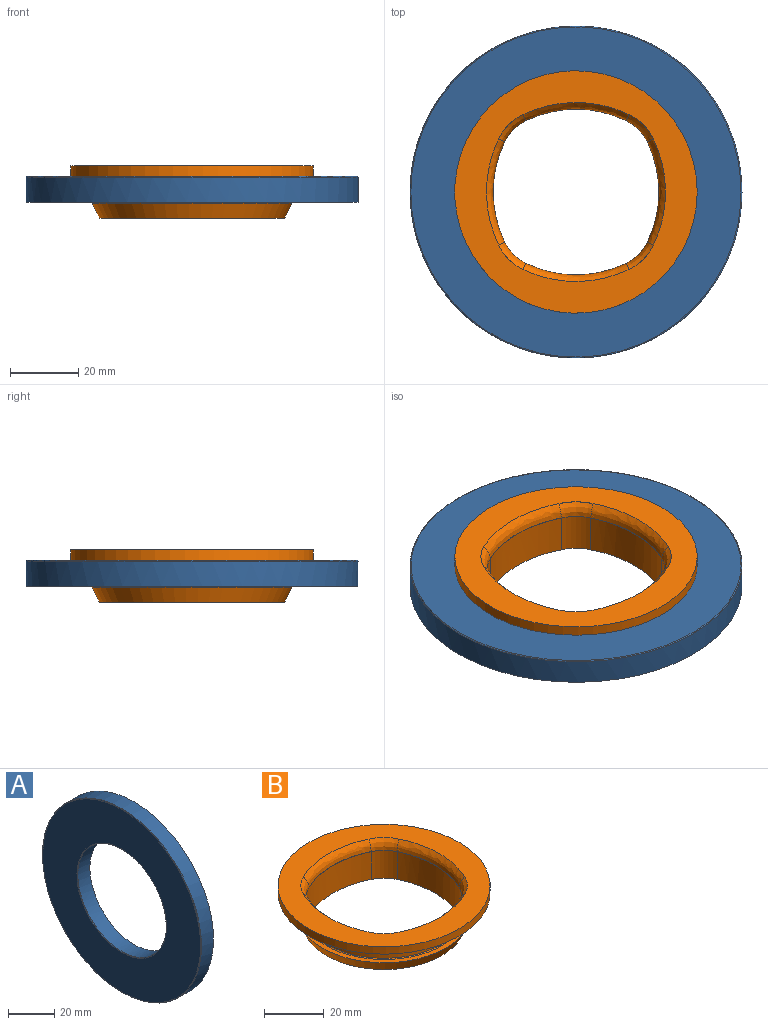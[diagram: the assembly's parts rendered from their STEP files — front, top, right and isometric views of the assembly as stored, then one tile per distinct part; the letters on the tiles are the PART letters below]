
ASSEMBLY  parts=2 mates=1
PART A: 12 faces, bbox 7.6x105x105 mm
  f0: plane 97.03x97.03mm, normal (1,0,0), area 230.5mm2, adj f1,f7
  f1: cylinder r=48.51mm len=97.03mm, axis (-1,0,0), area 2245.3mm2, adj f0,f8
  f2: plane 96.52x96.52mm, normal (-1,0,0), area 4974.6mm2, adj f8,f9
  f3: cylinder r=27.05mm len=54.1mm, axis (-1,0,0), area 1252mm2, adj f4,f9
  f4: plane 55.63x55.63mm, normal (1,0,0), area 131.3mm2, adj f3,f5
  f5: cylinder r=27.81mm len=55.63mm, axis (-1,0,0), area 1154.1mm2, adj f4,f10
  f6: plane 95x95mm, normal (1,0,0), area 4612.8mm2, adj f10,f11
  f7: cylinder r=47.75mm len=95.5mm, axis (-1,0,0), area 1981.4mm2, adj f0,f11
  f8: torus R=48.26mm, axis (1,0,0), area 121.4mm2, adj f1,f2
  f9: torus R=27.3mm, axis (1,0,0), area 68mm2, adj f2,f3
  f10: torus R=28.07mm, axis (-1,0,0), area 70mm2, adj f5,f6
  f11: torus R=47.5mm, axis (-1,0,0), area 119.5mm2, adj f6,f7
PART B: 42 faces, bbox 70.9x70.9x15.3 mm
  f0: bspline ~6.56x6.56mm, area 0mm2, adj f1,f41
  f1: plane 70.88x70.88mm, normal (0,0,1), area 1680.9mm2, adj f0,f2,f27,f28,f30,f31,f32,f34
  f2: cylinder r=35.43mm len=70.87mm, axis (0,0,1), area 667.3mm2, adj f1,f3
  f3: plane 70.87x70.87mm, normal (0,0,-1), area 1594.1mm2, adj f2,f4
  f4: torus R=27.35mm, axis (0,0,1), area 80.4mm2, adj f3,f5
  f5: cylinder r=27.05mm len=54.1mm, axis (0,0,1), area 1245mm2, adj f4,f6
  f6: torus R=27.35mm, axis (0,0,-1), area 80.4mm2, adj f5,f7
  f7: plane 58.42x58.42mm, normal (0,0,1), area 330.3mm2, adj f6,f8
  f8: cone r=27.05mm half-angle=26.6deg, axis (0,0,1), area 853.3mm2, adj f7,f9
  f9: plane 54.1x54.1mm, normal (0,0,-1), area 353.5mm2, adj f8,f10,f20,f21,f22,f23,f24,f25
  f10: cylinder r=33.53mm len=29.36mm, axis (0,0,1), area 344.7mm2, adj f9,f11,f20,f26
  f11: bspline ~31.43x5.95mm, area 0.4mm2, adj f10,f12,f18,f19
  f12: bspline ~8.43x8.43mm, area 0.1mm2, adj f11,f13,f18,f20
  f13: bspline ~31.43x5.95mm, area 0.4mm2, adj f12,f14,f18,f21
  f14: bspline ~8.43x8.43mm, area 0.1mm2, adj f13,f15,f18,f22
  f15: bspline ~31.43x5.95mm, area 0.4mm2, adj f14,f16,f18,f23
  f16: bspline ~8.43x8.43mm, area 0.1mm2, adj f15,f17,f18,f24
  f17: bspline ~31.43x5.95mm, area 0.4mm2, adj f16,f18,f19,f25
  f18: plane 48.46x48.46mm, normal (0,0,-1), area 2.2mm2, adj f11,f12,f13,f14,f15,f16,f17,f19
  f19: bspline ~8.43x8.43mm, area 0.1mm2, adj f11,f17,f18,f26
  f20: cylinder r=12.7mm len=11.34mm, axis (0,0,1), area 100.6mm2, adj f9,f10,f12,f21
  f21: cylinder r=33.53mm len=29.36mm, axis (0,0,1), area 344.7mm2, adj f9,f13,f20,f22
  f22: cylinder r=12.7mm len=11.34mm, axis (0,0,1), area 100.6mm2, adj f9,f14,f21,f23
  f23: cylinder r=33.53mm len=29.36mm, axis (0,0,1), area 344.7mm2, adj f9,f15,f22,f24
  f24: cylinder r=12.7mm len=11.34mm, axis (0,0,1), area 100.6mm2, adj f9,f16,f23,f25
  f25: cylinder r=33.53mm len=29.36mm, axis (0,0,1), area 344.7mm2, adj f9,f17,f24,f26
  f26: cylinder r=12.7mm len=11.34mm, axis (0,0,1), area 100.6mm2, adj f9,f10,f19,f25
  f27: bspline ~31.4x5.5mm, area 139.8mm2, adj f1,f18,f30,f40
  f28: bspline ~6.56x6.56mm, area 0mm2, adj f1,f29
  f29: bspline ~7.16x7.16mm, area 0mm2, adj f28,f30
  f30: bspline ~7.92x7.92mm, area 42.1mm2, adj f1,f18,f27,f29,f31
  f31: bspline ~31.4x5.5mm, area 139.8mm2, adj f1,f18,f30,f34
  f32: bspline ~6.56x6.56mm, area 0mm2, adj f1,f33
  f33: bspline ~7.16x7.16mm, area 0mm2, adj f32,f34
  f34: bspline ~7.92x7.92mm, area 42.1mm2, adj f1,f18,f31,f33,f35
  f35: bspline ~31.4x5.42mm, area 139.8mm2, adj f1,f18,f34,f38
  f36: bspline ~6.56x6.56mm, area 0mm2, adj f1,f37
  f37: bspline ~7.16x7.16mm, area 0mm2, adj f36,f38
  f38: bspline ~7.92x7.92mm, area 42.1mm2, adj f1,f18,f35,f37,f39
  f39: bspline ~31.4x5.5mm, area 139.8mm2, adj f1,f18,f38,f40
  f40: bspline ~7.92x7.92mm, area 42.1mm2, adj f1,f18,f27,f39,f41
  f41: bspline ~7.16x7.16mm, area 0mm2, adj f0,f40
PLACE A rot(axis=(0,1,0),90deg) t=(0,0,-3)mm
PLACE B at identity
MATE fastened A.f1 <-> B.f2  axis (0,0,1) through (0,0,-3)mm
